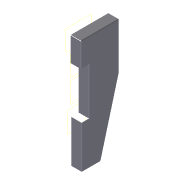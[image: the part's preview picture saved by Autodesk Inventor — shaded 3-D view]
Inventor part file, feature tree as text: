
AUTODESK INVENTOR PART (.ipt)
format: ipt  version: 2015 (Build 190159000, 159)  size: 195,072 bytes
history: native  units: mm
features: reference x8, sheet_metal_op x4, sketch x3, other x2, mirror x1
ambient origin geometry x8: Origin, YZ Plane, XZ Plane, XY Plane, X Axis, Y Axis, Z Axis, Center Point
bodies: Solid1 (feature_tree)
feature tree (18):
  sheet_metal_op  "Face1"
  sketch  "Sketch3"  dims[d16=445.0mm]
  sheet_metal_op  "Flange4"
  mirror  "Mirror1"
  sketch  "Sketch1"  dims[d1=1.6mm]
  reference  "Reference1"
  reference  "Reference2"
  other  "Plate1"
  reference  "Reference3"
  reference  "Reference4"
  reference  "Reference5"
  reference  "Reference6"
  reference  "Reference7"
  reference  "Reference8"
  sketch  "Sketch6"  dims[d17=35.0mm d18=50.0mm d19=3.922832mm d40=5.0mm d41=48.571429mm d42=5.0mm d43=5.0mm d44=1.6mm d45=0.8mm d46=3.2mm d47=1.6mm d48=40.0mm d49=90.0deg d50=1.6mm d51=6.4mm d52=1.6mm d53=1.6mm d54=150.0mm d55=75.0mm]
  other  "Plate5"
  sheet_metal_op  "Bend4"
  sheet_metal_op  "Corner4"
